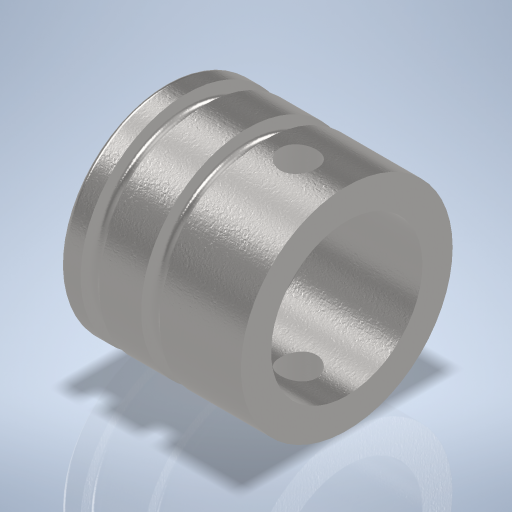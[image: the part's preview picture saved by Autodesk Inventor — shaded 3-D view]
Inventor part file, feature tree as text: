
AUTODESK INVENTOR PART (.ipt)
format: ipt  version: 2024 (Build 280153000, 153)  size: 397,312 bytes
history: native  units: mm
features: sketch x3, hole x2, fillet x2, revolve x1, plane x1
ambient origin geometry x8: Origin, YZ Plane, XZ Plane, XY Plane, X Axis, Y Axis, Z Axis, Center Point
bodies: Volumenkörper1 (feature_tree)
feature tree (9):
  revolve  "Umdrehung1"
  hole  "Bohrung1"  [1 undecoded]
  fillet  "Rundung1"  Radius=16.5mm
  fillet  "Rundung2"  Radius=26.5mm
  plane  "Arbeitsebene13"
  hole  "Bohrung4"  [1 undecoded]
  sketch  "Skizze1"  dims[d0=35.0mm d1=30.01mm d3=16.5mm d4=26.5mm]
  sketch  "Skizze2"  dims[d5=30.0mm d6=3.1mm]
  sketch  "Skizze17"  dims[d7=90.0deg d8=25.0mm d9=16.0mm d10=4.0mm d11=2.0mm d12=90.0deg d13=17.5mm d14=20.594885mm d15=1.0mm d16=1.0mm d50=0.0mm d51=8.0mm d52=5.98mm d53=6.0mm d54=4.0mm d55=2.0mm d56=90.0deg d57=8.0mm d58=0.0mm]
note: 2 required parameter values undecoded (feature->parameter linkage not recoverable at this tier; creation-order binding heuristic only, values carry confidence <= 0.55)
